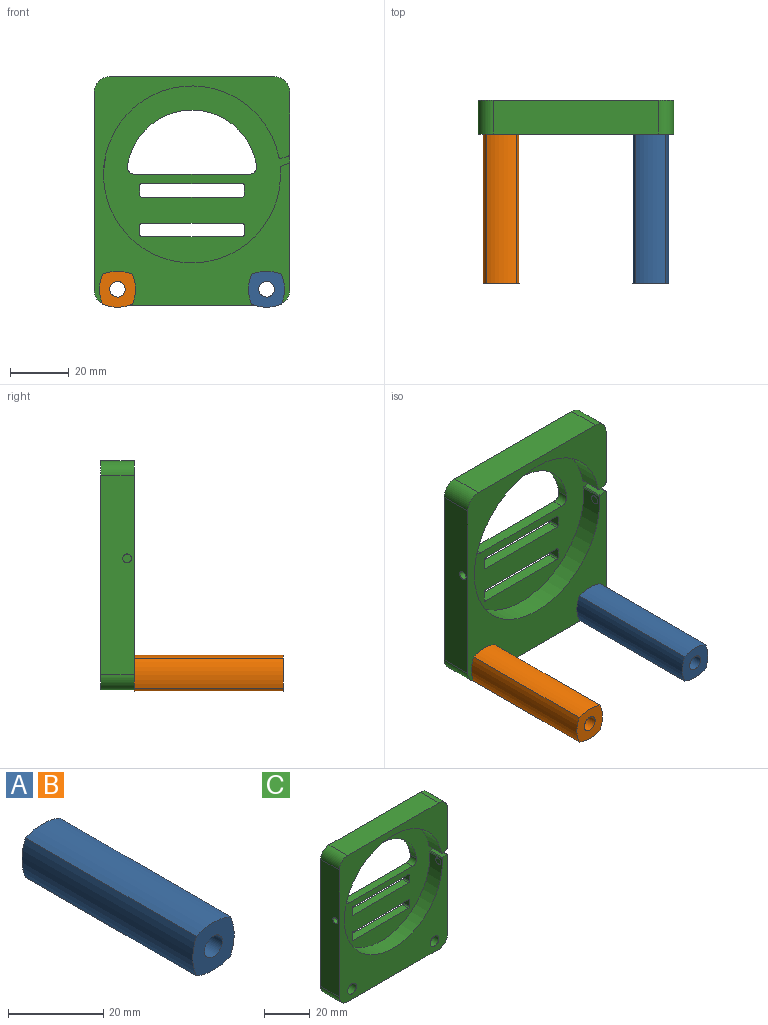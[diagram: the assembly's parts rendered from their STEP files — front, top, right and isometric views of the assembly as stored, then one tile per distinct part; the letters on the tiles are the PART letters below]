
ASSEMBLY  parts=3 mates=2
PART A: 7 faces, bbox 12.3x50.8x12.3 mm
  f0: cylinder r=12.7mm len=50.8mm, axis (0,1,0), area 531mm2, adj f1,f3,f5,f6
  f1: cylinder r=12.7mm len=50.8mm, axis (0,1,0), area 531mm2, adj f0,f2,f5,f6
  f2: cylinder r=12.7mm len=50.8mm, axis (0,1,0), area 531mm2, adj f1,f3,f5,f6
  f3: cylinder r=12.7mm len=50.8mm, axis (0,1,0), area 531mm2, adj f0,f2,f5,f6
  f4: cylinder r=2.64mm len=50.8mm, axis (0,1,0), area 843.2mm2, adj f5,f6
  f5: plane 12.28x12.28mm, normal (0,-1,0), area 110.3mm2, adj f0,f1,f2,f3,f4
  f6: plane 12.28x12.28mm, normal (0,1,0), area 110.3mm2, adj f0,f1,f2,f3,f4
PART B: same geometry as A
PART C: 43 faces, bbox 66.5x11.4x78 mm
  f0: cylinder r=22.23mm len=43.98mm, axis (0,-1,0), area 241.4mm2, adj f1,f2,f3,f4
  f1: plane 77.98x66.55mm, normal (0,1,0), area 4039.7mm2, adj f0,f2,f4,f5,f6,f7,f8,f9
  f2: cylinder r=2.54mm len=3.81mm, axis (0,-1,0), area 16.6mm2, adj f0,f1,f3,f21
  f3: plane 63.44x60.33mm, normal (0,-1,0), area 1784.4mm2, adj f0,f2,f4,f5,f6,f7,f8,f9
  f4: cylinder r=2.54mm len=3.81mm, axis (0,-1,0), area 16.6mm2, adj f0,f1,f3,f21
  f5: plane 34.29x3.81mm, normal (0,0,-1), area 130.6mm2, adj f1,f3,f6,f12
  f6: cylinder r=0.64mm len=3.81mm, axis (0,-1,0), area 3.8mm2, adj f1,f3,f5,f7
  f7: plane 3.81x3.3mm, normal (1,0,0), area 12.6mm2, adj f1,f3,f6,f8
  f8: cylinder r=0.64mm len=3.81mm, axis (0,1,0), area 3.8mm2, adj f1,f3,f7,f9
  f9: plane 34.29x3.81mm, normal (0,0,1), area 130.6mm2, adj f1,f3,f8,f10
  f10: cylinder r=0.64mm len=3.81mm, axis (0,-1,0), area 3.8mm2, adj f1,f3,f9,f11
  f11: plane 3.81x3.3mm, normal (-1,0,0), area 12.6mm2, adj f1,f3,f10,f12
  f12: cylinder r=0.64mm len=3.81mm, axis (0,1,0), area 3.8mm2, adj f1,f3,f5,f11
  f13: plane 34.29x3.81mm, normal (0,0,-1), area 130.6mm2, adj f1,f3,f14,f20
  f14: cylinder r=0.64mm len=3.81mm, axis (0,-1,0), area 3.8mm2, adj f1,f3,f13,f15
  f15: plane 3.81x3.3mm, normal (1,0,0), area 12.6mm2, adj f1,f3,f14,f16
  f16: cylinder r=0.64mm len=3.81mm, axis (0,1,0), area 3.8mm2, adj f1,f3,f15,f17
  f17: plane 34.29x3.81mm, normal (0,0,1), area 130.6mm2, adj f1,f3,f16,f18
  f18: cylinder r=0.64mm len=3.81mm, axis (0,-1,0), area 3.8mm2, adj f1,f3,f17,f19
  f19: plane 3.81x3.3mm, normal (-1,0,0), area 12.6mm2, adj f1,f3,f18,f20
  f20: cylinder r=0.64mm len=3.81mm, axis (0,1,0), area 3.8mm2, adj f1,f3,f13,f19
  f21: plane 38.95x3.81mm, normal (0,0,1), area 148.4mm2, adj f1,f2,f3,f4
  f22: cylinder r=2.67mm len=11.43mm, axis (0,-1,0), area 191.5mm2, adj f1,f39
  f23: cylinder r=2.67mm len=11.43mm, axis (0,-1,0), area 191.5mm2, adj f1,f39
  f24: plane 56.39x11.43mm, normal (0,0,-1), area 644.5mm2, adj f1,f25,f31,f39
  f25: cylinder r=5.08mm len=11.43mm, axis (0,1,0), area 91.2mm2, adj f1,f24,f26,f39
  f26: plane 67.82x11.43mm, normal (-1,0,0), area 768mm2, adj f1,f25,f27,f39,f40
  f27: cylinder r=5.08mm len=11.43mm, axis (0,-1,0), area 91.2mm2, adj f1,f26,f28,f39
  f28: plane 56.39x11.43mm, normal (0,0,1), area 644.5mm2, adj f1,f27,f29,f39
  f29: cylinder r=5.08mm len=11.43mm, axis (0,1,0), area 91.2mm2, adj f1,f28,f30,f39
  f30: plane 67.82x11.43mm, normal (1,0,0), area 740.4mm2, adj f1,f3,f29,f31,f32,f38,f39,f41
  f31: cylinder r=5.08mm len=11.43mm, axis (0,-1,0), area 91.2mm2, adj f1,f24,f30,f39
  f32: cylinder r=0.51mm len=7.62mm, axis (0,1,0), area 4.9mm2, adj f3,f30,f33,f39
  f33: plane 7.62x2.67mm, normal (0.29,0,-0.96), area 21.3mm2, adj f3,f32,f34,f39
  f34: cylinder r=0.51mm len=7.62mm, axis (0,-1,0), area 6.5mm2, adj f3,f33,f35,f39
  f35: cylinder r=30.16mm len=60.33mm, axis (0,-1,0), area 1410.1mm2, adj f3,f34,f36,f39,f40
  f36: cylinder r=0.51mm len=7.62mm, axis (0,-1,0), area 5.1mm2, adj f3,f35,f37,f39
  f37: plane 7.62x2.19mm, normal (-0.32,0,0.95), area 17.6mm2, adj f3,f36,f38,f39
  f38: cylinder r=0.51mm len=7.62mm, axis (0,1,0), area 7.3mm2, adj f3,f30,f37,f39
  f39: plane 77.98x66.55mm, normal (0,-1,0), area 2255.3mm2, adj f22,f23,f24,f25,f26,f27,f28,f29
  f40: cylinder r=1.51mm len=3.15mm, axis (1,0,0), area 29.7mm2, adj f26,f35
  f41: cylinder r=1.51mm len=3.15mm, axis (1,0,0), area 29.7mm2, adj f30,f42
  f42: cylinder r=30.16mm len=3.02mm, axis (0,-1,0), area 7.2mm2, adj f41
PLACE A t=(26.98,-1.88,-29.03)mm
PLACE B t=(-23.82,-1.88,-29.03)mm
PLACE C t=(1.58,9.55,4.39)mm
MATE cylindrical A.f4 <-> C.f23  axis (0,1,0) through (26.98,-1.88,-29.03)mm
MATE cylindrical B.f4 <-> C.f22  axis (0,1,0) through (-23.82,-1.88,-29.03)mm
